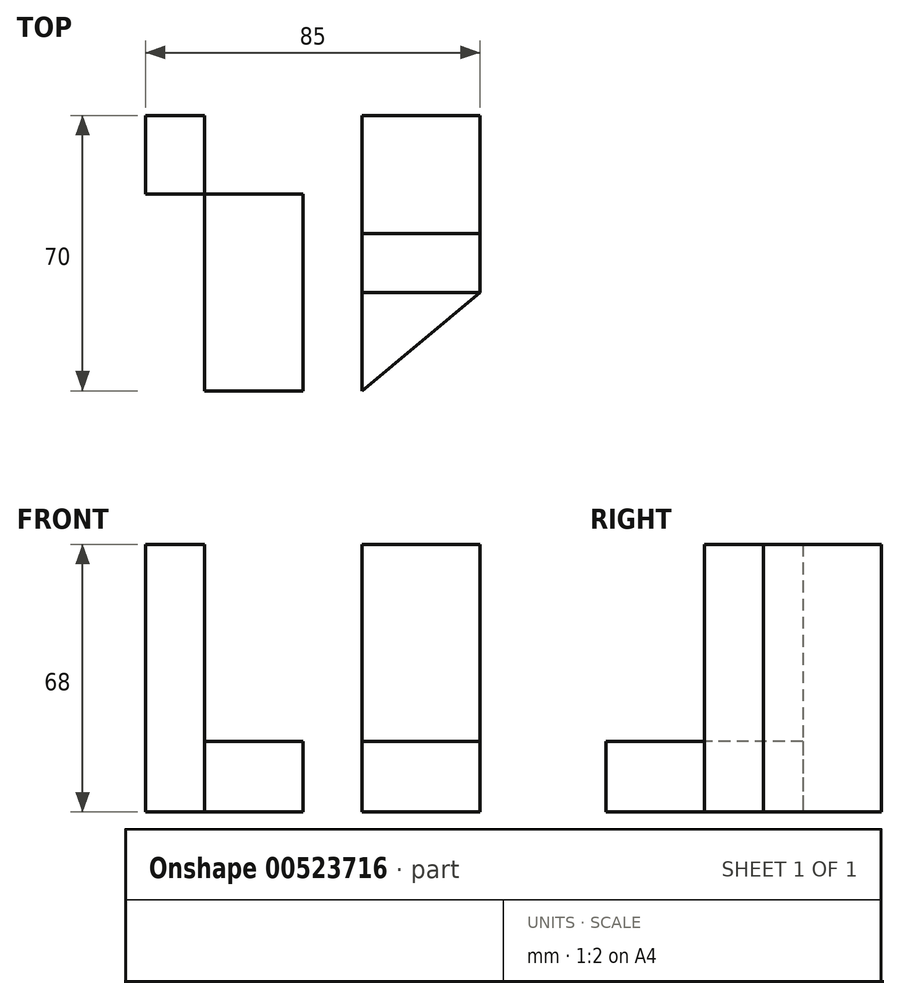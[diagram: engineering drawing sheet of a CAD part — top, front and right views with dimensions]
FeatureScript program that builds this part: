
annotation { "Feature Type Name" : "Feature", "Feature Type Description" : "" }
export const myFeature = defineFeature(function(context is Context, id is Id, definition is map)
    precondition{}
    {
        {
            var Q0;
            Q0=qCreatedBy(makeId("Top.planeOp"),FACE);
            var sketch = newSketch(context, id + "F0", { "sketchPlane" : qUnion([Q0])});
            skLineSegment(sketch, "E0.bottom", {"start": v(0, 0) * mm, "end": v(15, 0) * mm});
            skLineSegment(sketch, "E0.top", {"start": v(0, 70) * mm, "end": v(85, 70) * mm});
            skLineSegment(sketch, "E0.left", {"start": v(0, 0) * mm, "end": v(0, 70) * mm});
            skLineSegment(sketch, "E0.right", {"start": v(85, 25) * mm, "end": v(85, 70) * mm});
            skLineSegment(sketch, "E1.bottom", {"start": v(0, 70) * mm, "end": v(15, 70) * mm});
            skLineSegment(sketch, "E1.left", {"start": v(0, 70) * mm, "end": v(0, 0) * mm});
            skLineSegment(sketch, "E1.right", {"start": v(15, 70) * mm, "end": v(15, 0) * mm});
            skLineSegment(sketch, "E2", {"start": v(85, 70) * mm, "end": v(85, 55) * mm});
            skLineSegment(sketch, "E3", {"start": v(85, 55) * mm, "end": v(85, 25) * mm});
            skLineSegment(sketch, "E4", {"start": v(0, 0) * mm, "end": v(55, 0) * mm});
            skLineSegment(sketch, "E5", {"start": v(55, 0) * mm, "end": v(85, 25) * mm});
            skLineSegment(sketch, "E6", {"start": v(85, 70) * mm, "end": v(55, 70) * mm});
            skLineSegment(sketch, "E7", {"start": v(55, 0) * mm, "end": v(55, 70) * mm});
            skLineSegment(sketch, "E8", {"start": v(0, 70) * mm, "end": v(0, 50) * mm});
            skLineSegment(sketch, "E9", {"start": v(55, 0) * mm, "end": v(40, 0) * mm});
            skLineSegment(sketch, "E10", {"start": v(40, 0) * mm, "end": v(40, 50) * mm});
            skLineSegment(sketch, "E11", {"start": v(40, 50) * mm, "end": v(0, 50) * mm});
            skLineSegment(sketch, "E12", {"start": v(85, 25) * mm, "end": v(55, 25) * mm});
            skLineSegment(sketch, "E13", {"start": v(85, 25) * mm, "end": v(85, 40) * mm});
            skLineSegment(sketch, "E14", {"start": v(85, 40) * mm, "end": v(55, 40) * mm});
            skSolve(sketch);
        }
        {
            var Q0;
            {var subQ5=sQuery(id+"F0.wireOp",EDGE,"E10");Q0=makeQuery(id+"F0.imprint","IMPRINT",FACE,{"disambiguationData":[TD([[makeQuery(id+"F0.imprint","IMPRINT",EDGE,{"derivedFrom":subQ5}),1.0]])]});}
            var Q1;
            {var subQ0=sQuery(id+"F0.wireOp",EDGE,"E5");Q1=makeQuery(id+"F0.imprint","IMPRINT",FACE,{"disambiguationData":[TD([[makeQuery(id+"F0.imprint","IMPRINT",EDGE,{"derivedFrom":subQ0}),1.0]])]});}
            var Q2;
            Q2=makeQuery(id+"F0.imprint","IMPRINT",FACE,{"disambiguationData":[TD([[makeQuery(id+"F0.imprint","IMPRINT",EDGE,{"derivedFrom":sQuery(id+"F0.wireOp",EDGE,"E2")}),-1.0]])]});
            extrude(context, id + "F1", {"entities" : qUnion([Q0, Q1, Q2]), "depth" : 18 * mm, "offsetDistance" : 25 * mm});
        }
        {
            var Q0;
            {var subQ4=sQuery(id+"F0.wireOp",EDGE,"E0.top");Q0=makeQuery(id+"F0.imprint","IMPRINT",FACE,{"disambiguationData":[TD([[makeQuery(id+"F0.imprint","IMPRINT",EDGE,{"derivedFrom":subQ4}),-1.0]])]});}
            var Q1;
            {var subQ0=sQuery(id+"F0.wireOp",EDGE,"E1.left");Q1=makeQuery(id+"F0.imprint","IMPRINT",FACE,{"disambiguationData":[TD([[makeQuery(id+"F0.imprint","IMPRINT",EDGE,{"derivedFrom":subQ0}),1.0]])]});}
            var Q2;
            {var subQ0=sQuery(id+"F0.wireOp",EDGE,"E1.bottom");Q2=makeQuery(id+"F0.imprint","IMPRINT",FACE,{"disambiguationData":[TD([[makeQuery(id+"F0.imprint","IMPRINT",EDGE,{"derivedFrom":subQ0}),-1.0]])]});}
            extrude(context, id + "F2", {"entities" : qUnion([Q0, Q1, Q2]), "depth" : 68 * mm, "offsetDistance" : 25 * mm});
        }
        {
            var Q0;
            Q0=makeQuery(id+"F2.opExtrude","SWEPT_FACE",FACE,{"disambiguationData":[OSD([sQuery(id+"F0.wireOp",EDGE,"E7")])]});
            var sketch = newSketch(context, id + "F3", { "sketchPlane" : qUnion([Q0])});
            skLineSegment(sketch, "E15", {"start": v(0, 0) * mm, "end": v(25, 0) * mm});
            skLineSegment(sketch, "E16", {"start": v(25, 0) * mm, "end": v(35, 0) * mm});
            skLineSegment(sketch, "E17", {"start": v(35, 0) * mm, "end": v(40, 0) * mm});
            skLineSegment(sketch, "E18", {"start": v(25, 0) * mm, "end": v(25, 68) * mm});
            skLineSegment(sketch, "E19", {"start": v(25, 68) * mm, "end": v(40, 68) * mm});
            skLineSegment(sketch, "E20", {"start": v(40, 68) * mm, "end": v(40, 0) * mm});
            skLineSegment(sketch, "E21.0", {"start": v(55, 0) * mm, "end": v(25, 0) * mm});
            skLineSegment(sketch, "E22.0.0", {"start": v(25, 0) * mm, "end": v(40, 0) * mm});
            skLineSegment(sketch, "E22.0.2", {"start": v(40, 0) * mm, "end": v(25, 0) * mm});
            skSolve(sketch);
        }
        {
            var Q0;
            {var subQ0=sQuery(id+"F0.wireOp",EDGE,"E12");Q0=makeQuery(id+"F0.imprint","IMPRINT",FACE,{"disambiguationData":[TD([[makeQuery(id+"F0.imprint","IMPRINT",EDGE,{"derivedFrom":subQ0}),-1.0]])]});}
            var sketch = newSketch(context, id + "F4", { "sketchPlane" : qUnion([Q0])});
            skLineSegment(sketch, "E23.0.0", {"start": v(85, 25) * mm, "end": v(85, 40) * mm});
            skLineSegment(sketch, "E23.0.1", {"start": v(85, 40) * mm, "end": v(55, 40) * mm});
            skLineSegment(sketch, "E23.0.2", {"start": v(55, 40) * mm, "end": v(55, 25) * mm});
            skLineSegment(sketch, "E23.0.3", {"start": v(55, 25) * mm, "end": v(85, 25) * mm});
            skLineSegment(sketch, "E24.0", {"start": v(55, 25) * mm, "end": v(55, 40) * mm});
            skPoint(sketch, "E25.0", {"position": v(55, 40) * mm});
            skLineSegment(sketch, "E26.0.0", {"start": v(55, 0) * mm, "end": v(55, 25) * mm});
            skLineSegment(sketch, "E26.0.2", {"start": v(55, 25) * mm, "end": v(55, 0) * mm});
            skLineSegment(sketch, "E27.0", {"start": v(55, 0) * mm, "end": v(85, 25) * mm});
            skLineSegment(sketch, "E28.0.0", {"start": v(85, 25) * mm, "end": v(55, 25) * mm});
            skSolve(sketch);
        }
        {
            var Q0;
            Q0=makeQuery(id+"F4.imprint","IMPRINT",FACE,{"disambiguationData":[TD([[makeQuery(id+"F4.imprint","IMPRINT",EDGE,{"derivedFrom":sQuery(id+"F4.wireOp",EDGE,"E23.0.0")}),1.0]])]});
            extrude(context, id + "F5", {"entities" : qUnion([Q0]), "depth" : 68 * mm, "offsetDistance" : 25 * mm});
        }
    });
